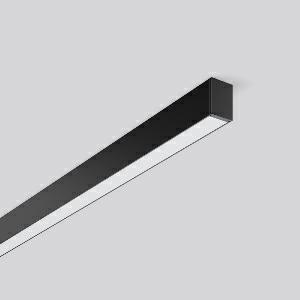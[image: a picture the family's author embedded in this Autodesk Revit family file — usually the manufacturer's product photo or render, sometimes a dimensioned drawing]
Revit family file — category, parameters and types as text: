
# Revit family: less_is_more_27_312198_003_1_76_4c85
name_source: partatom
category: Lighting Fixtures
units: mm (PartAtom-declared; Revit-internal decimal feet)

## family parameters
Cut with Voids When Loaded = No
Host = Face
Light Source = No
Part Type = Normal
Room Calculation Point = No
Round Connector Dimension = Use Diameter
Shared = No

## types (1)
- LESS IS MORE 27 (1 x LED Modul 840, 1900 lm, 4000)
    Apparent Load = 31 VA
    CIE Flux Codes = 48 79 96 100 100
    Color Rendering = 80
    Color Temperature = 4000
    Default Elevation = 1800 mm
    Description = Series: LESS IS MORE 27
Ceiling and wall luminaire with slim design. Housing: extruded aluminium profile, powder-coated. End cap aluminium powder-coated. Diffuser made of non-yellowing plastic (PMMA), opal. Suitable for Ceiling mounting, Wall (surface). External driver with connecting cable. 
Colour: deep black, matt (RAL 9005)
Length: 1212 mm
Width: 28 mm
Height: 38 mm
Lamp: LED
Socket: without socket
Colour temperature: 4000K
Colour rendering index (CRI): 82
System power: 31 W
Rated luminous flux: 1900 lm
Luminous efficiency: 61 lm/W
Control gear: Voltage converter, DALI dim.
Protection class: II
Type of protection: IP 20
    Height = 38 mm
    Lamp = 1 x LED Modul 840
    Lamp Light Flux = 1900 lm
    Lamp count = 1
    Length = 1212 mm
    Lifetime = 50000 h
    Luminous efficacy = 61 lm/W
    Manufacturer = RZB
    ModVariant = No
    Model = 312198.003.1.76
    Mounting Place = Ceiling, Wall
    Mounting Type = Surface mounted
    Number of Poles = 1
    OnlyDefault = Yes
    Power Factor = 1
    Product Name = LESS IS MORE 27
    Product group = Surface mounted LED linear luminaires
    ProductGroupID = 307
    Protection Class = Protection class II
    Protection Degree = IP 20
    RLX_Detail_Level = 1
    RLX_Emergency_Light_Flux = 0 lm
    RLX_Emergency_Type = 0
    RLX_Emergency_Type_DB = No
    RlxData = <blob elided: 28709 chars, md5=16b7c843>
    Socket = socket
    Standby Power = 0 W
    System Light Flux = 1900 lm
    System Power = 31 W
    Type Comments = Product without accessories
    Type Image = 312196.003.jpg
    URL = http://relux.com
    VarID = ---
    Voltage = 230 V
    Voltage Range = 220-240 V
    Weight = 0.00 kg
    Width = 28 mm

## geometry (parser evidence)
native form markers: Blend x4, Sweep x10
no freeform markers — native parametric forms only
